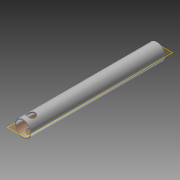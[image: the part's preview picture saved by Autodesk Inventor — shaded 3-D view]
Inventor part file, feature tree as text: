
AUTODESK INVENTOR PART (.ipt)
format: ipt  version: 2014 (Build 180170000, 170)  size: 94,208 bytes
history: native  units: in
note: dims shown in document units (in); Inventor stores cm internally (conversion verified against a paired STEP export)
features: extrude x2, sketch x2
ambient origin geometry x8: Origin, YZ Plane, XZ Plane, XY Plane, X Axis, Y Axis, Z Axis, Center Point
bodies: Solid1 (feature_tree)
feature tree (4):
  extrude  "Extrusion1"  Depth=0.875in
  extrude  "Extrusion2"  Depth=0.5in
  sketch  "Sketch1"  dims[d0=1.0in d1=0.875in]
  sketch  "Sketch2"  dims[d2=8.25in d3=0.0in d4=0.5in d5=7.75in d6=1.0in d7=0.0in]
